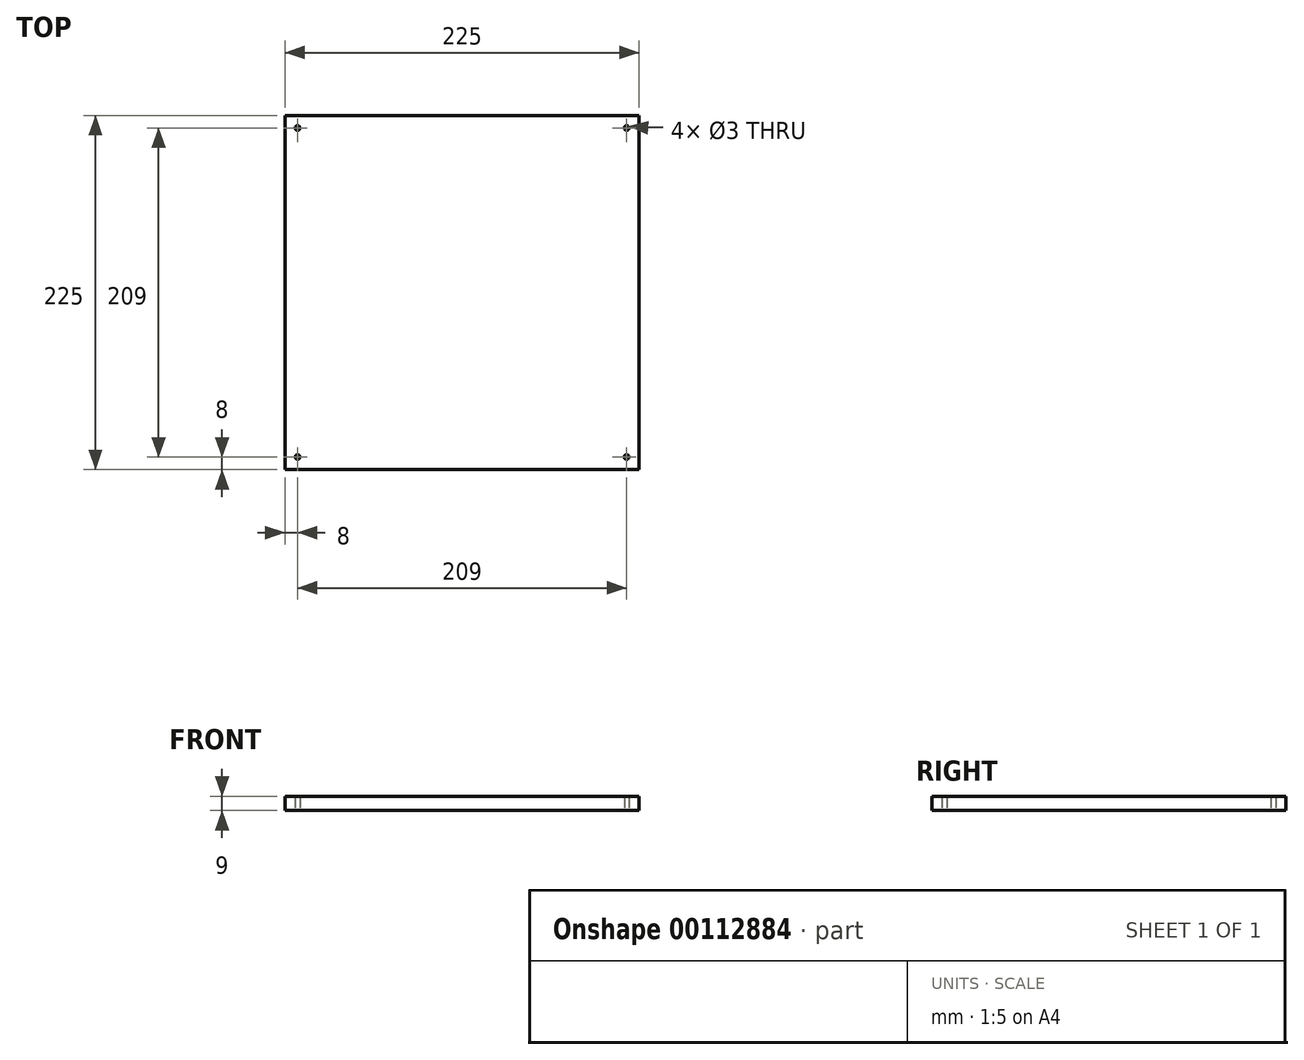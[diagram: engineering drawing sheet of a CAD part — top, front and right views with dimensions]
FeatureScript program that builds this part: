
annotation { "Feature Type Name" : "Feature", "Feature Type Description" : "" }
export const myFeature = defineFeature(function(context is Context, id is Id, definition is map)
    precondition{}
    {
        {
            var Q0;
            Q0=qCreatedBy(makeId("Top.planeOp"),FACE);
            var sketch = newSketch(context, id + "F0", { "sketchPlane" : qUnion([Q0])});
            skLineSegment(sketch, "E0.bottom", {"start": v(112.5, 112.5) * mm, "end": v(-112.5, 112.5) * mm});
            skLineSegment(sketch, "E0.top", {"start": v(112.5, -112.5) * mm, "end": v(-112.5, -112.5) * mm});
            skLineSegment(sketch, "E0.left", {"start": v(112.5, 112.5) * mm, "end": v(112.5, -112.5) * mm});
            skLineSegment(sketch, "E0.right", {"start": v(-112.5, 112.5) * mm, "end": v(-112.5, -112.5) * mm});
            skPoint(sketch, "E0.middle", {"position": v(0, 0) * mm});
            skLineSegment(sketch, "E1.bottom", {"start": v(-104.5, 104.5) * mm, "end": v(104.5, 104.5) * mm, "construction": true});
            skLineSegment(sketch, "E1.top", {"start": v(-104.5, -104.5) * mm, "end": v(104.5, -104.5) * mm, "construction": true});
            skLineSegment(sketch, "E1.left", {"start": v(-104.5, 104.5) * mm, "end": v(-104.5, -104.5) * mm, "construction": true});
            skLineSegment(sketch, "E1.right", {"start": v(104.5, 104.5) * mm, "end": v(104.5, -104.5) * mm, "construction": true});
            skSolve(sketch);
        }
        {
            var Q0;
            Q0=makeQuery(id+"F0.imprint","IMPRINT",FACE,{"disambiguationData":[TD([[makeQuery(id+"F0.imprint","IMPRINT",EDGE,{"derivedFrom":sQuery(id+"F0.wireOp",EDGE,"E0.bottom")}),1.0]])]});
            extrude(context, id + "F1", {"entities" : qUnion([Q0]), "depth" : 9 * mm});
        }
        {
            var Q0;
            Q0=sQuery(id+"F0.wireOp",VERTEX,"E1.left.start");
            var Q1;
            Q1=sQuery(id+"F0.wireOp",VERTEX,"E1.right.start");
            var Q2;
            Q2=sQuery(id+"F0.wireOp",VERTEX,"E1.left.end");
            var Q3;
            Q3=sQuery(id+"F0.wireOp",VERTEX,"E1.right.end");
            var Q4;
            Q4=makeQuery(id+"F1.opExtrude","SWEPT_BODY",BODY,{"disambiguationData":[OSD([sQuery(id+"F0.wireOp",EDGE,"E0.bottom"),sQuery(id+"F0.wireOp",EDGE,"E0.top"),sQuery(id+"F0.wireOp",EDGE,"E0.left"),sQuery(id+"F0.wireOp",EDGE,"E0.right")])]});
            hole(context, id + "F2", {"style" : HoleStyle.SIMPLE, "endStyle" : HoleEndStyle.THROUGH, "oppositeDirection" : true, "holeDiameter" : 3 * mm, "startFromSketch" : true, "locations" : qUnion([Q0, Q1, Q2, Q3]), "scope" : qUnion([Q4]), "isTappedThrough" : true});
        }
    });
